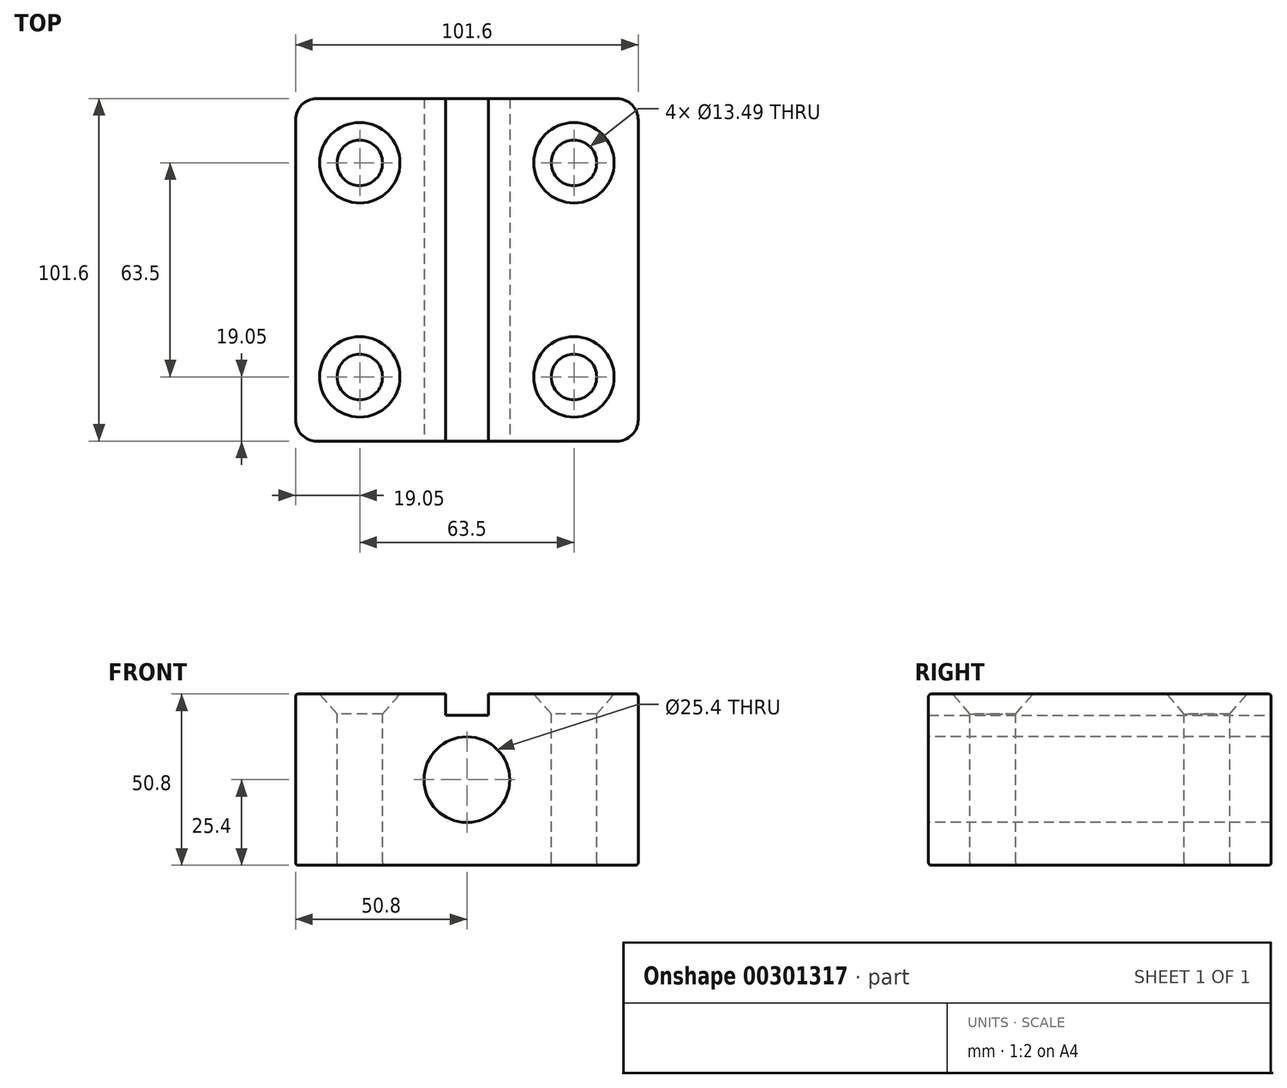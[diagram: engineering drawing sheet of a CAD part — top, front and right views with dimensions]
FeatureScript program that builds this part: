
annotation { "Feature Type Name" : "Feature", "Feature Type Description" : "" }
export const myFeature = defineFeature(function(context is Context, id is Id, definition is map)
    precondition{}
    {
        {
            var Q0;
            Q0=qCreatedBy(makeId("Front.planeOp"),FACE);
            var sketch = newSketch(context, id + "F0", { "sketchPlane" : qUnion([Q0])});
            skLineSegment(sketch, "E0.bottom", {"start": v(-50.8, 25.4) * mm, "end": v(50.8, 25.4) * mm});
            skLineSegment(sketch, "E0.top", {"start": v(-50.8, -25.4) * mm, "end": v(50.8, -25.4) * mm});
            skLineSegment(sketch, "E0.left", {"start": v(-50.8, 25.4) * mm, "end": v(-50.8, -25.4) * mm});
            skLineSegment(sketch, "E0.right", {"start": v(50.8, 25.4) * mm, "end": v(50.8, -25.4) * mm});
            skLineSegment(sketch, "E1.bottom", {"start": v(-6.35, 25.4) * mm, "end": v(6.35, 25.4) * mm});
            skLineSegment(sketch, "E1.top", {"start": v(-6.35, 19.05) * mm, "end": v(6.35, 19.05) * mm});
            skLineSegment(sketch, "E1.left", {"start": v(-6.35, 25.4) * mm, "end": v(-6.35, 19.05) * mm});
            skLineSegment(sketch, "E1.right", {"start": v(6.35, 25.4) * mm, "end": v(6.35, 19.05) * mm});
            skSolve(sketch);
        }
        {
            var Q0;
            Q0=makeQuery(id+"F0.imprint","IMPRINT",FACE,{"disambiguationData":[TD([[makeQuery(id+"F0.imprint","IMPRINT",EDGE,{"derivedFrom":sQuery(id+"F0.wireOp",EDGE,"E0.bottom")}),-1.0]])]});
            extrude(context, id + "F1", {"entities" : qUnion([Q0]), "endBound" : BoundingType.SYMMETRIC, "depth" : 101.6 * mm});
        }
        {
            var Q0;
            Q0=makeQuery(id+"F1.opExtrude","SWEPT_FACE",FACE,{"disambiguationData":[OSD([sQuery(id+"F0.wireOp",EDGE,"E0.bottom")])]});
            var sketch = newSketch(context, id + "F2", { "sketchPlane" : qUnion([Q0])});
            skPoint(sketch, "E2", {"position": v(-31.75, 31.75) * mm});
            skPoint(sketch, "E3.MirrorP", {"position": v(31.75, 31.75) * mm});
            skPoint(sketch, "E4.MirrorP", {"position": v(-31.75, -31.75) * mm});
            skPoint(sketch, "E5.MirrorP", {"position": v(31.75, -31.75) * mm});
            skSolve(sketch);
        }
        {
            var Q0;
            Q0=sQuery(id+"F2.wireOp",VERTEX,"E2");
            var Q1;
            Q1=sQuery(id+"F2.wireOp",VERTEX,"E3.MirrorP");
            var Q2;
            Q2=sQuery(id+"F2.wireOp",VERTEX,"E4.MirrorP");
            var Q3;
            Q3=sQuery(id+"F2.wireOp",VERTEX,"E5.MirrorP");
            var Q4;
            Q4=makeQuery(id+"F1.opExtrude","SWEPT_BODY",BODY,{"disambiguationData":[OSD([sQuery(id+"F0.wireOp",EDGE,"E0.bottom"),sQuery(id+"F0.wireOp",EDGE,"E0.top"),sQuery(id+"F0.wireOp",EDGE,"E0.left"),sQuery(id+"F0.wireOp",EDGE,"E0.right")])]});
            hole(context, id + "F3", {"style" : HoleStyle.C_SINK, "endStyle" : HoleEndStyle.THROUGH, "standardTappedOrClearance" : lookupTablePath({ "standard" : "ANSI", "fit" : "Normal (ASME)", "size" : "1/2", "type" : "Clearance" }), "standardBlindInLast" : lookupTablePath({ "fit" : "Free", "standard" : "ANSI", "size" : "1/2", "type" : "Clearance" }), "holeDiameter" : 13.5 * mm, "cSinkDiameter" : 23.83 * mm, "cSinkAngle" : 82 * degree, "tappedDepth" : 12.7 * mm, "tapClearance" : 3, "locations" : qUnion([Q0, Q1, Q2, Q3]), "scope" : qUnion([Q4])});
        }
        {
            var Q0;
            Q0=makeQuery(id+"F1.opExtrude","SWEPT_EDGE",EDGE,{"disambiguationData":[OSD([sQuery(id+"F0.wireOp",EDGE,"E0.bottom"),sQuery(id+"F0.wireOp",EDGE,"E0.left")])]});
            var Q1;
            Q1=makeQuery(id+"F1.opExtrude","CAP_EDGE",EDGE,{"disambiguationData":[OSD([sQuery(id+"F0.wireOp",EDGE,"E0.bottom")])],"isStart":true});
            var Q2;
            Q2=makeQuery(id+"F1.opExtrude","SWEPT_EDGE",EDGE,{"disambiguationData":[OSD([sQuery(id+"F0.wireOp",EDGE,"E0.bottom"),sQuery(id+"F0.wireOp",EDGE,"E0.right")])]});
            var Q3;
            Q3=makeQuery(id+"F1.opExtrude","CAP_EDGE",EDGE,{"disambiguationData":[OSD([sQuery(id+"F0.wireOp",EDGE,"E0.bottom")])],"isStart":false});
            var Q4;
            Q4=makeQuery(id+"F1.opExtrude","SWEPT_FACE",FACE,{"disambiguationData":[OSD([sQuery(id+"F0.wireOp",EDGE,"E0.top")])]});
            fillet(context, id + "F4", {"entities" : qUnion([Q0, Q1, Q2, Q3, Q4]), "radius" : 0.81 * mm, "tangentPropagation" : true, "allowEdgeOverflow" : false});
        }
        {
            var Q0;
            Q0=makeQuery(id+"F1.opExtrude","CAP_EDGE",EDGE,{"disambiguationData":[OSD([sQuery(id+"F0.wireOp",EDGE,"E0.left")])],"isStart":false});
            var Q1;
            Q1=makeQuery(id+"F1.opExtrude","CAP_EDGE",EDGE,{"disambiguationData":[OSD([sQuery(id+"F0.wireOp",EDGE,"E0.right")])],"isStart":false});
            var Q2;
            Q2=makeQuery(id+"F1.opExtrude","CAP_EDGE",EDGE,{"disambiguationData":[OSD([sQuery(id+"F0.wireOp",EDGE,"E0.left")])],"isStart":true});
            var Q3;
            Q3=makeQuery(id+"F1.opExtrude","CAP_EDGE",EDGE,{"disambiguationData":[OSD([sQuery(id+"F0.wireOp",EDGE,"E0.right")])],"isStart":true});
            fillet(context, id + "F5", {"entities" : qUnion([Q0, Q1, Q2, Q3]), "radius" : 6.35 * mm, "tangentPropagation" : true, "allowEdgeOverflow" : false});
        }
        {
            var Q0;
            Q0=makeQuery(id+"F1.opExtrude","CAP_FACE",FACE,{"disambiguationData":[OSD([sQuery(id+"F0.wireOp",EDGE,"E0.bottom"),sQuery(id+"F0.wireOp",EDGE,"E0.top"),sQuery(id+"F0.wireOp",EDGE,"E0.left"),sQuery(id+"F0.wireOp",EDGE,"E0.right")])],"isStart":false});
            var sketch = newSketch(context, id + "F6", { "sketchPlane" : qUnion([Q0])});
            skPoint(sketch, "E6", {"position": v(0, 0) * mm});
            skSolve(sketch);
        }
        {
            var Q0;
            Q0=sQuery(id+"F6.wireOp",VERTEX,"E6");
            var Q1;
            Q1=makeQuery(id+"F1.opExtrude","SWEPT_BODY",BODY,{"disambiguationData":[OSD([sQuery(id+"F0.wireOp",EDGE,"E0.bottom"),sQuery(id+"F0.wireOp",EDGE,"E0.top"),sQuery(id+"F0.wireOp",EDGE,"E0.left"),sQuery(id+"F0.wireOp",EDGE,"E0.right")])]});
            hole(context, id + "F7", {"style" : HoleStyle.SIMPLE, "endStyle" : HoleEndStyle.THROUGH, "holeDiameter" : 25.4 * mm, "tappedDepth" : 12.7 * mm, "tapClearance" : 3, "locations" : qUnion([Q0]), "scope" : qUnion([Q1])});
        }
    });
